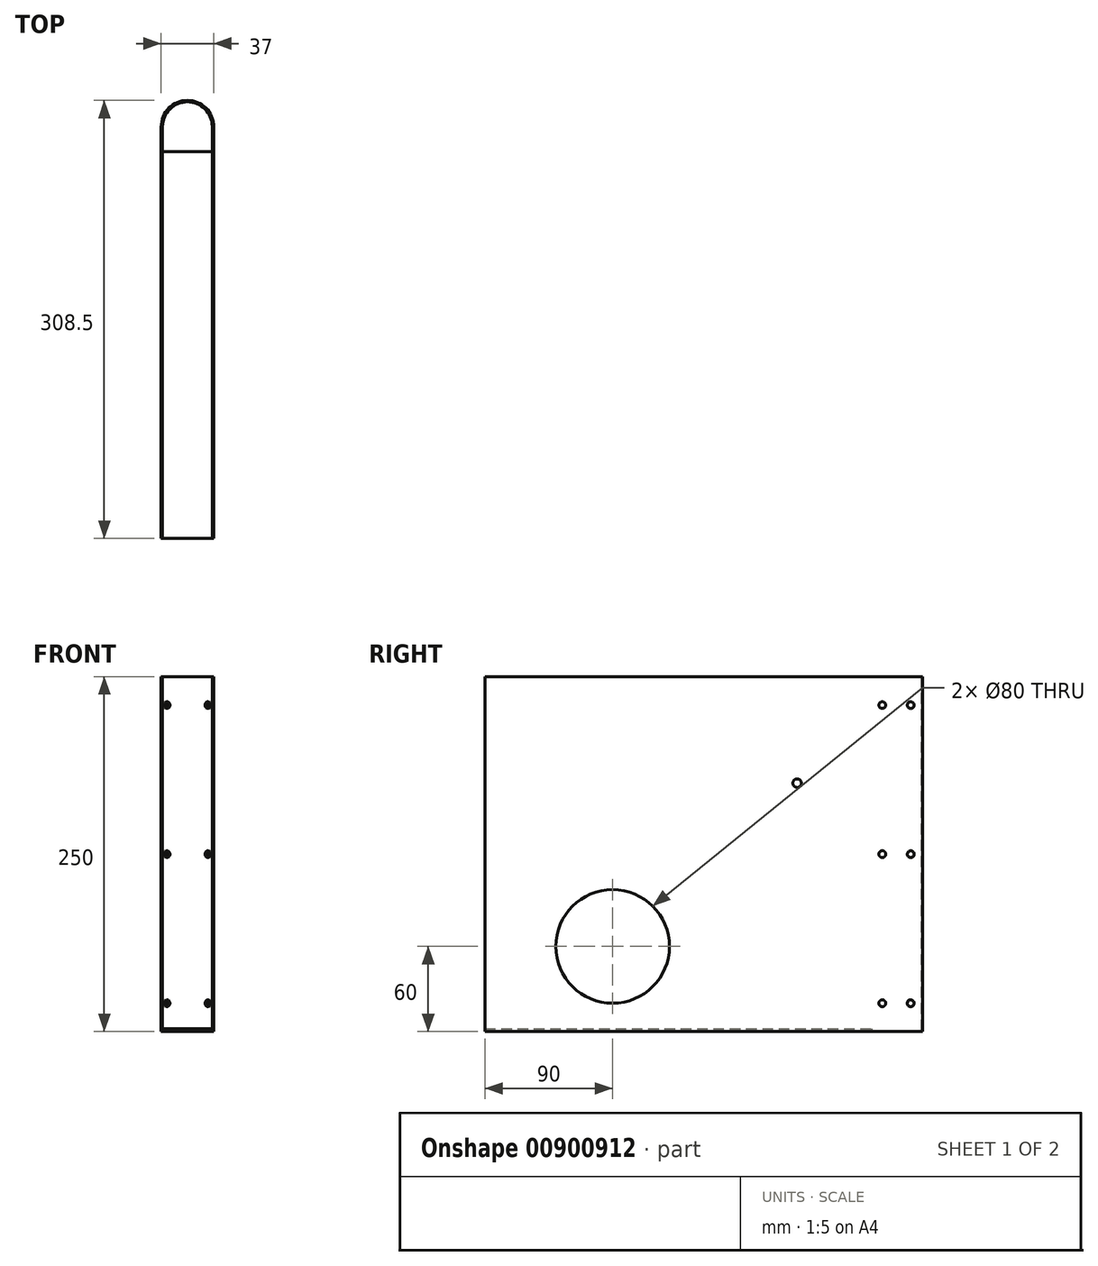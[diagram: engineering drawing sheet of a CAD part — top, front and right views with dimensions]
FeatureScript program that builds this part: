
annotation { "Feature Type Name" : "Feature", "Feature Type Description" : "" }
export const myFeature = defineFeature(function(context is Context, id is Id, definition is map)
    precondition{}
    {
        {
            var Q0;
            Q0=qCreatedBy(makeId("Top.planeOp"),FACE);
            var sketch = newSketch(context, id + "F0", { "sketchPlane" : qUnion([Q0])});
            skArc(sketch, "E0", {"start": v(18.5, 0) * mm, "mid": v(0, 18.5) * mm, "end": v(-18.5, 0) * mm});
            skLineSegment(sketch, "E1", {"start": v(-36.42, 0) * mm, "end": v(-18.5, 0) * mm});
            skArc(sketch, "E2", {"start": v(17.5, 0) * mm, "mid": v(0, 17.5) * mm, "end": v(-17.5, 0) * mm});
            skLineSegment(sketch, "E3.trimOffspring", {"start": v(-17.5, 0) * mm, "end": v(17.5, 0) * mm});
            skLineSegment(sketch, "E4.trimOffspring", {"start": v(18.5, 0) * mm, "end": v(37.4, 0) * mm});
            skLineSegment(sketch, "E5", {"start": v(-18.5, 0) * mm, "end": v(-18.5, -290) * mm});
            skLineSegment(sketch, "E6", {"start": v(18.5, 0) * mm, "end": v(18.5, -290) * mm});
            skLineSegment(sketch, "E7", {"start": v(-17.5, 0) * mm, "end": v(-17.5, -290) * mm});
            skLineSegment(sketch, "E8", {"start": v(17.5, 0) * mm, "end": v(17.5, -290) * mm});
            skLineSegment(sketch, "E9", {"start": v(-18.5, -290) * mm, "end": v(-17.5, -290) * mm});
            skLineSegment(sketch, "E10", {"start": v(17.5, -290) * mm, "end": v(18.5, -290) * mm});
            skLineSegment(sketch, "E11", {"start": v(0, 17.5) * mm, "end": v(0, -17.5) * mm});
            skSolve(sketch);
        }
        {
            var Q0;
            {var subQ0=sQuery(id+"F0.wireOp",EDGE,"E0");Q0=makeQuery(id+"F0.imprint","IMPRINT",FACE,{"disambiguationData":[TD([[makeQuery(id+"F0.imprint","IMPRINT",EDGE,{"derivedFrom":subQ0}),1.0]])]});}
            extrude(context, id + "F1", {"entities" : qUnion([Q0]), "depth" : 250 * mm, "offsetDistance" : 25 * mm});
        }
        {
            var Q0;
            Q0=makeQuery(id+"F1.opExtrude","SWEPT_FACE",FACE,{"disambiguationData":[OSD([sQuery(id+"F0.wireOp",EDGE,"E5")])]});
            var sketch = newSketch(context, id + "F2", { "sketchPlane" : qUnion([Q0])});
            skLineSegment(sketch, "E12.bottom", {"start": v(17.5, 0) * mm, "end": v(290, 0) * mm});
            skLineSegment(sketch, "E12.top", {"start": v(17.5, 2) * mm, "end": v(290, 2) * mm});
            skLineSegment(sketch, "E12.left", {"start": v(17.5, 0) * mm, "end": v(17.5, 2) * mm});
            skLineSegment(sketch, "E12.right", {"start": v(290, 0) * mm, "end": v(290, 2) * mm});
            skSolve(sketch);
        }
        {
            var Q0;
            Q0 = qSketchRegion(id + "F2", true);
            extrude(context, id + "F3", {"entities" : qUnion([Q0]), "operationType" : NewBodyOperationType.ADD, "oppositeDirection" : true, "depth" : 37 * mm, "offsetDistance" : 25 * mm});
        }
        {
            var Q0;
            Q0=makeQuery(id+"F1.opExtrude","SWEPT_FACE",FACE,{"disambiguationData":[OSD([sQuery(id+"F0.wireOp",EDGE,"E5")])]});
            var sketch = newSketch(context, id + "F4", { "sketchPlane" : qUnion([Q0])});
            skLineSegment(sketch, "E13", {"start": v(145, 250) * mm, "end": v(145, 0) * mm});
            skLineSegment(sketch, "E14", {"start": v(290, 175) * mm, "end": v(0, 175) * mm});
            skCircle(sketch, "E15", {"center": v(70, 175) * mm, "radius": 3 * mm});
            skLineSegment(sketch, "E16", {"start": v(0, 60) * mm, "end": v(290, 60) * mm});
            skCircle(sketch, "E17", {"center": v(200, 60) * mm, "radius": 40 * mm});
            skPoint(sketch, "E18.orphan", {"position": v(0, 125) * mm});
            skPoint(sketch, "E19.end.orphan", {"position": v(290, 125) * mm});
            skSolve(sketch);
        }
        {
            var Q0;
            Q0 = qSketchRegion(id + "F4", true);
            extrude(context, id + "F5", {"entities" : qUnion([Q0]), "operationType" : NewBodyOperationType.REMOVE, "endBound" : BoundingType.THROUGH_ALL, "oppositeDirection" : true, "depth" : 25 * mm, "offsetDistance" : 25 * mm});
        }
        {
            var Q0;
            Q0=qCreatedBy(makeId("Right.planeOp"),FACE);
            var sketch = newSketch(context, id + "F6", { "sketchPlane" : qUnion([Q0])});
            skLineSegment(sketch, "E20", {"start": v(0, 0) * mm, "end": v(0, 20) * mm});
            skCircle(sketch, "E21", {"center": v(-10, 20) * mm, "radius": 2.4 * mm});
            skCircle(sketch, "E22", {"center": v(10, 20) * mm, "radius": 2.4 * mm});
            skCircle(sketch, "E23", {"center": v(-10, 125) * mm, "radius": 2.4 * mm});
            skCircle(sketch, "E24", {"center": v(10, 125) * mm, "radius": 2.4 * mm});
            skLineSegment(sketch, "E25", {"start": v(10, 125) * mm, "end": v(-10, 125) * mm});
            skCircle(sketch, "E26.MirrorC", {"center": v(10, 230) * mm, "radius": 2.4 * mm});
            skCircle(sketch, "E27.MirrorC", {"center": v(-10, 230) * mm, "radius": 2.4 * mm});
            skSolve(sketch);
        }
        {
            var Q0;
            Q0 = qSketchRegion(id + "F6", true);
            extrude(context, id + "F7", {"entities" : qUnion([Q0]), "operationType" : NewBodyOperationType.REMOVE, "oppositeDirection" : true, "depth" : 25 * mm, "offsetDistance" : 25 * mm, "hasSecondDirection" : true, "secondDirectionOppositeDirection" : false, "secondDirectionDepth" : 25 * mm});
        }
    });
